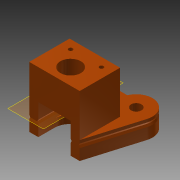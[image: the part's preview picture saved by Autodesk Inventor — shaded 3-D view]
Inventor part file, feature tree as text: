
AUTODESK INVENTOR PART (.ipt)
format: ipt  version: 2013 (Build 170138000, 138)  size: 293,376 bytes
history: native  units: mm
features: sketch x12, extrude x11, projected_geometry x5, plane x1, sweep x1, mirror x1
ambient origin geometry x8: Origin, YZ Plane, XZ Plane, XY Plane, X Axis, Y Axis, Z Axis, Center Point
bodies: Solid1 (feature_tree)
feature tree (31):
  extrude  "Extrusion1"  Depth=25.0mm
  extrude  "Extrusion10"  Depth=4.0mm TaperAngle=0.0deg
  extrude  "Extrusion11"  Depth=25.0mm
  extrude  "Extrusion12"  Depth=26.0mm TaperAngle=0.0deg
  extrude  "Extrusion13"  Depth=8.0mm
  extrude  "Extrusion14"  Depth=4.0mm TaperAngle=0.0deg
  extrude  "Extrusion15"  Depth=10.16mm
  extrude  "Extrusion16"  Depth=2.0mm
  extrude  "Extrusion17"  Depth=7.633mm
  plane  "Work Plane1"
  sweep  "Sweep1"
  extrude  "Extrusion18"  [1 undecoded]
  mirror  "Mirror2"
  extrude  "Extrusion19"  Depth=2.0mm
  sketch  "Sketch12"  dims[d0=16.0mm d2=25.0mm]
  sketch  "Sketch13"  dims[d3=5.2mm d4=4.0mm d5=0.0mm]
  sketch  "Sketch14"  dims[d44=20.0mm d45=25.0mm]
  sketch  "Sketch16"  dims[d46=5.0mm d47=0.0mm d48=26.0mm d49=0.0mm]
  projected_geometry  "Projected Loop4"
  sketch  "Sketch17"  dims[d50=8.0mm d51=8.0mm]
  projected_geometry  "Projected Loop5"
  projected_geometry  "Projected Loop6"
  sketch  "Sketch18"  dims[d52=15.0mm d53=0.0mm d54=4.0mm d55=0.0mm]
  sketch  "Sketch19"  dims[d56=5.0mm d57=0.0mm d58=10.16mm]
  sketch  "Sketch20"  dims[d60=8.0mm d61=2.0mm]
  projected_geometry  "Projected Loop7"
  sketch  "Sketch21"  dims[d62=7.633mm d63=7.633mm]
  sketch  "Sketch22"  dims[d64=15.0mm d65=0.0mm d66=15.0mm d67=0.0mm]
  sketch  "Sketch23"  dims[d68=15.0mm d69=0.0mm d70=-2.5mm]
  sketch  "Sketch24"  dims[d71=0.5mm d73=2.0mm d74=0.0mm d75=15.0mm d76=0.0mm d77=0.3mm d78=0.0mm]
  projected_geometry  "Project Cut Edges2"
note: 1 required parameter value undecoded (feature->parameter linkage not recoverable at this tier; creation-order binding heuristic only, values carry confidence <= 0.55)
